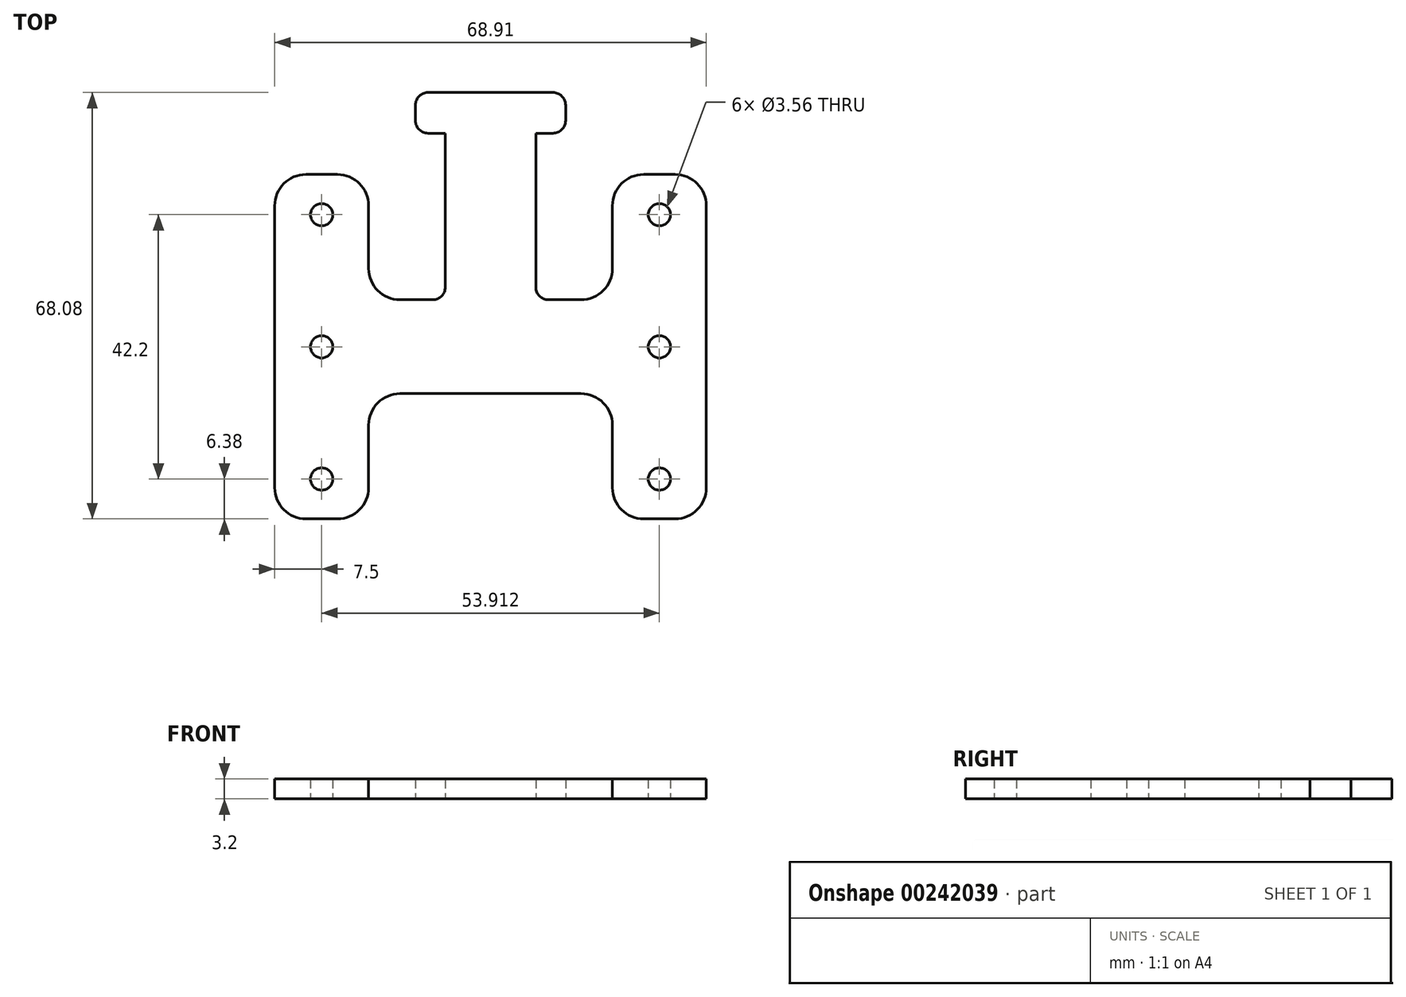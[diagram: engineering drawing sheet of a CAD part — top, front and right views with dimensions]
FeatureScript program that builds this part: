
annotation { "Feature Type Name" : "Feature", "Feature Type Description" : "" }
export const myFeature = defineFeature(function(context is Context, id is Id, definition is map)
    precondition{}
    {
        {
            var Q0;
            Q0=qCreatedBy(makeId("Top.planeOp"),FACE);
            var sketch = newSketch(context, id + "F0", { "sketchPlane" : qUnion([Q0])});
            skLineSegment(sketch, "E0.bottom", {"start": v(5, 0) * mm, "end": v(10, 0) * mm});
            skLineSegment(sketch, "E0.top", {"start": v(5, 55) * mm, "end": v(10, 55) * mm});
            skLineSegment(sketch, "E0.left", {"start": v(0, 5) * mm, "end": v(0, 50) * mm});
            skLineSegment(sketch, "E0.right", {"start": v(15, 5) * mm, "end": v(15, 15) * mm});
            skLineSegment(sketch, "E1", {"start": v(15, 27.5) * mm, "end": v(26.27, 27.5) * mm, "construction": true});
            skPoint(sketch, "E1.endSnap0", {"position": v(15, 27.5) * mm});
            skLineSegment(sketch, "E2.bottom", {"start": v(20, 20) * mm, "end": v(34.46, 20) * mm});
            skLineSegment(sketch, "E2.top", {"start": v(20, 35) * mm, "end": v(25.23, 35) * mm});
            skLineSegment(sketch, "E2.left", {"start": v(15, 27.48) * mm, "end": v(15, 27.5) * mm});
            skCircle(sketch, "E3", {"center": v(7.5, 27.48) * mm, "radius": 1.78 * mm});
            skCircle(sketch, "E4.0.1.0", {"center": v(7.5, 48.58) * mm, "radius": 1.78 * mm});
            skLineSegment(sketch, "E4.direction1", {"start": v(7.5, 27.48) * mm, "end": v(32.5, 27.48) * mm, "construction": true});
            skLineSegment(sketch, "E4.direction2", {"start": v(7.5, 27.48) * mm, "end": v(7.5, 48.58) * mm, "construction": true});
            skCircle(sketch, "E5.MirrorC", {"center": v(7.5, 6.38) * mm, "radius": 1.78 * mm});
            skLineSegment(sketch, "E6.trimOffspring", {"start": v(15, 40) * mm, "end": v(15, 50) * mm});
            skPoint(sketch, "E7.visualSharp", {"position": v(15, 35) * mm});
            skArc(sketch, "E7.filletArc", {"start": v(15, 40) * mm, "mid": v(16.46, 36.46) * mm, "end": v(20, 35) * mm});
            skPoint(sketch, "E8.visualSharp", {"position": v(15, 55) * mm});
            skArc(sketch, "E8.filletArc", {"start": v(15, 50) * mm, "mid": v(13.54, 53.54) * mm, "end": v(10, 55) * mm});
            skPoint(sketch, "E9.visualSharp", {"position": v(0, 55) * mm});
            skArc(sketch, "E9.filletArc", {"start": v(5, 55) * mm, "mid": v(1.46, 53.54) * mm, "end": v(0, 50) * mm});
            skPoint(sketch, "E10.visualSharp", {"position": v(0, 0) * mm});
            skArc(sketch, "E10.filletArc", {"start": v(0, 5) * mm, "mid": v(1.46, 1.46) * mm, "end": v(5, 0) * mm});
            skPoint(sketch, "E11.visualSharp", {"position": v(15, 0) * mm});
            skArc(sketch, "E11.filletArc", {"start": v(10, 0) * mm, "mid": v(13.54, 1.46) * mm, "end": v(15, 5) * mm});
            skPoint(sketch, "E12.visualSharp", {"position": v(15, 20) * mm});
            skArc(sketch, "E12.filletArc", {"start": v(20, 20) * mm, "mid": v(16.46, 18.54) * mm, "end": v(15, 15) * mm});
            skLineSegment(sketch, "E13", {"start": v(27.23, 37) * mm, "end": v(27.23, 61.58) * mm});
            skLineSegment(sketch, "E14", {"start": v(27.23, 61.58) * mm, "end": v(24.47, 61.58) * mm});
            skLineSegment(sketch, "E15", {"start": v(22.47, 63.58) * mm, "end": v(22.47, 66.08) * mm});
            skLineSegment(sketch, "E16", {"start": v(24.47, 68.08) * mm, "end": v(34.46, 68.08) * mm});
            skPoint(sketch, "E17.visualSharp", {"position": v(22.47, 68.08) * mm});
            skArc(sketch, "E17.filletArc", {"start": v(24.47, 68.08) * mm, "mid": v(23.06, 67.5) * mm, "end": v(22.47, 66.08) * mm});
            skPoint(sketch, "E18.visualSharp", {"position": v(22.47, 61.58) * mm});
            skArc(sketch, "E18.filletArc", {"start": v(22.47, 63.58) * mm, "mid": v(23.06, 62.17) * mm, "end": v(24.47, 61.58) * mm});
            skPoint(sketch, "E19.orphan", {"position": v(34.46, 35) * mm});
            skPoint(sketch, "E20.visualSharp", {"position": v(27.23, 35) * mm});
            skArc(sketch, "E20.filletArc", {"start": v(25.23, 35) * mm, "mid": v(26.64, 35.59) * mm, "end": v(27.23, 37) * mm});
            skLineSegment(sketch, "E21", {"start": v(34.46, 20) * mm, "end": v(34.46, 35) * mm, "construction": true});
            skLineSegment(sketch, "E22.MirrorCS", {"start": v(53.91, 27.48) * mm, "end": v(53.91, 27.5) * mm});
            skLineSegment(sketch, "E23.MirrorCS", {"start": v(46.44, 63.58) * mm, "end": v(46.44, 66.08) * mm});
            skLineSegment(sketch, "E24.MirrorCS", {"start": v(41.68, 61.58) * mm, "end": v(44.44, 61.58) * mm});
            skArc(sketch, "E25.MirrorCS", {"start": v(43.68, 35) * mm, "mid": v(42.27, 35.59) * mm, "end": v(41.68, 37) * mm});
            skArc(sketch, "E26.MirrorCS", {"start": v(46.44, 63.58) * mm, "mid": v(45.86, 62.17) * mm, "end": v(44.44, 61.58) * mm});
            skArc(sketch, "E27.MirrorCS", {"start": v(44.44, 68.08) * mm, "mid": v(45.86, 67.5) * mm, "end": v(46.44, 66.08) * mm});
            skLineSegment(sketch, "E28.MirrorCS", {"start": v(53.91, 27.5) * mm, "end": v(42.64, 27.5) * mm, "construction": true});
            skPoint(sketch, "E29.MirrorP", {"position": v(68.91, 0) * mm});
            skPoint(sketch, "E30.MirrorP", {"position": v(53.91, 35) * mm});
            skCircle(sketch, "E31.MirrorC", {"center": v(61.41, 48.58) * mm, "radius": 1.78 * mm});
            skCircle(sketch, "E32.MirrorC", {"center": v(61.41, 6.38) * mm, "radius": 1.78 * mm});
            skLineSegment(sketch, "E33.MirrorCS", {"start": v(63.91, 0) * mm, "end": v(58.91, 0) * mm});
            skPoint(sketch, "E34.MirrorP", {"position": v(53.91, 0) * mm});
            skLineSegment(sketch, "E35.MirrorCS", {"start": v(48.91, 20) * mm, "end": v(34.46, 20) * mm});
            skLineSegment(sketch, "E36.MirrorCS", {"start": v(48.91, 35) * mm, "end": v(43.68, 35) * mm});
            skLineSegment(sketch, "E37.MirrorCS", {"start": v(53.91, 40) * mm, "end": v(53.91, 50) * mm});
            skLineSegment(sketch, "E38.MirrorCS", {"start": v(63.91, 55) * mm, "end": v(58.91, 55) * mm});
            skArc(sketch, "E39.MirrorCS", {"start": v(63.91, 55) * mm, "mid": v(67.45, 53.54) * mm, "end": v(68.91, 50) * mm});
            skArc(sketch, "E40.MirrorCS", {"start": v(68.91, 5) * mm, "mid": v(67.45, 1.46) * mm, "end": v(63.91, 0) * mm});
            skPoint(sketch, "E41.MirrorP", {"position": v(68.91, 55) * mm});
            skPoint(sketch, "E42.MirrorP", {"position": v(53.91, 55) * mm});
            skArc(sketch, "E43.MirrorCS", {"start": v(53.91, 40) * mm, "mid": v(52.45, 36.46) * mm, "end": v(48.91, 35) * mm});
            skPoint(sketch, "E44.MirrorP", {"position": v(53.91, 27.5) * mm});
            skPoint(sketch, "E45.MirrorP", {"position": v(46.44, 68.08) * mm});
            skLineSegment(sketch, "E46.MirrorCS", {"start": v(61.41, 27.48) * mm, "end": v(36.41, 27.48) * mm, "construction": true});
            skPoint(sketch, "E47.MirrorP", {"position": v(46.44, 61.58) * mm});
            skArc(sketch, "E48.MirrorCS", {"start": v(53.91, 50) * mm, "mid": v(55.38, 53.54) * mm, "end": v(58.91, 55) * mm});
            skCircle(sketch, "E49.MirrorC", {"center": v(61.41, 27.48) * mm, "radius": 1.78 * mm});
            skPoint(sketch, "E50.MirrorP", {"position": v(41.68, 35) * mm});
            skPoint(sketch, "E51.MirrorP", {"position": v(53.91, 20) * mm});
            skLineSegment(sketch, "E52.MirrorCS", {"start": v(61.41, 27.48) * mm, "end": v(61.41, 48.58) * mm, "construction": true});
            skLineSegment(sketch, "E53.MirrorCS", {"start": v(41.68, 37) * mm, "end": v(41.68, 61.58) * mm});
            skArc(sketch, "E54.MirrorCS", {"start": v(48.91, 20) * mm, "mid": v(52.45, 18.54) * mm, "end": v(53.91, 15) * mm});
            skLineSegment(sketch, "E55.MirrorCS", {"start": v(53.91, 5) * mm, "end": v(53.91, 15) * mm});
            skLineSegment(sketch, "E56.MirrorCS", {"start": v(44.44, 68.08) * mm, "end": v(34.46, 68.08) * mm});
            skArc(sketch, "E57.MirrorCS", {"start": v(58.91, 0) * mm, "mid": v(55.38, 1.46) * mm, "end": v(53.91, 5) * mm});
            skLineSegment(sketch, "E58.MirrorCS", {"start": v(68.91, 5) * mm, "end": v(68.91, 50) * mm});
            skSolve(sketch);
        }
        {
            var Q0;
            Q0 = qSketchRegion(id + "F0", true);
            extrude(context, id + "F1", {"entities" : qUnion([Q0]), "depth" : 3.2 * mm});
        }
    });
